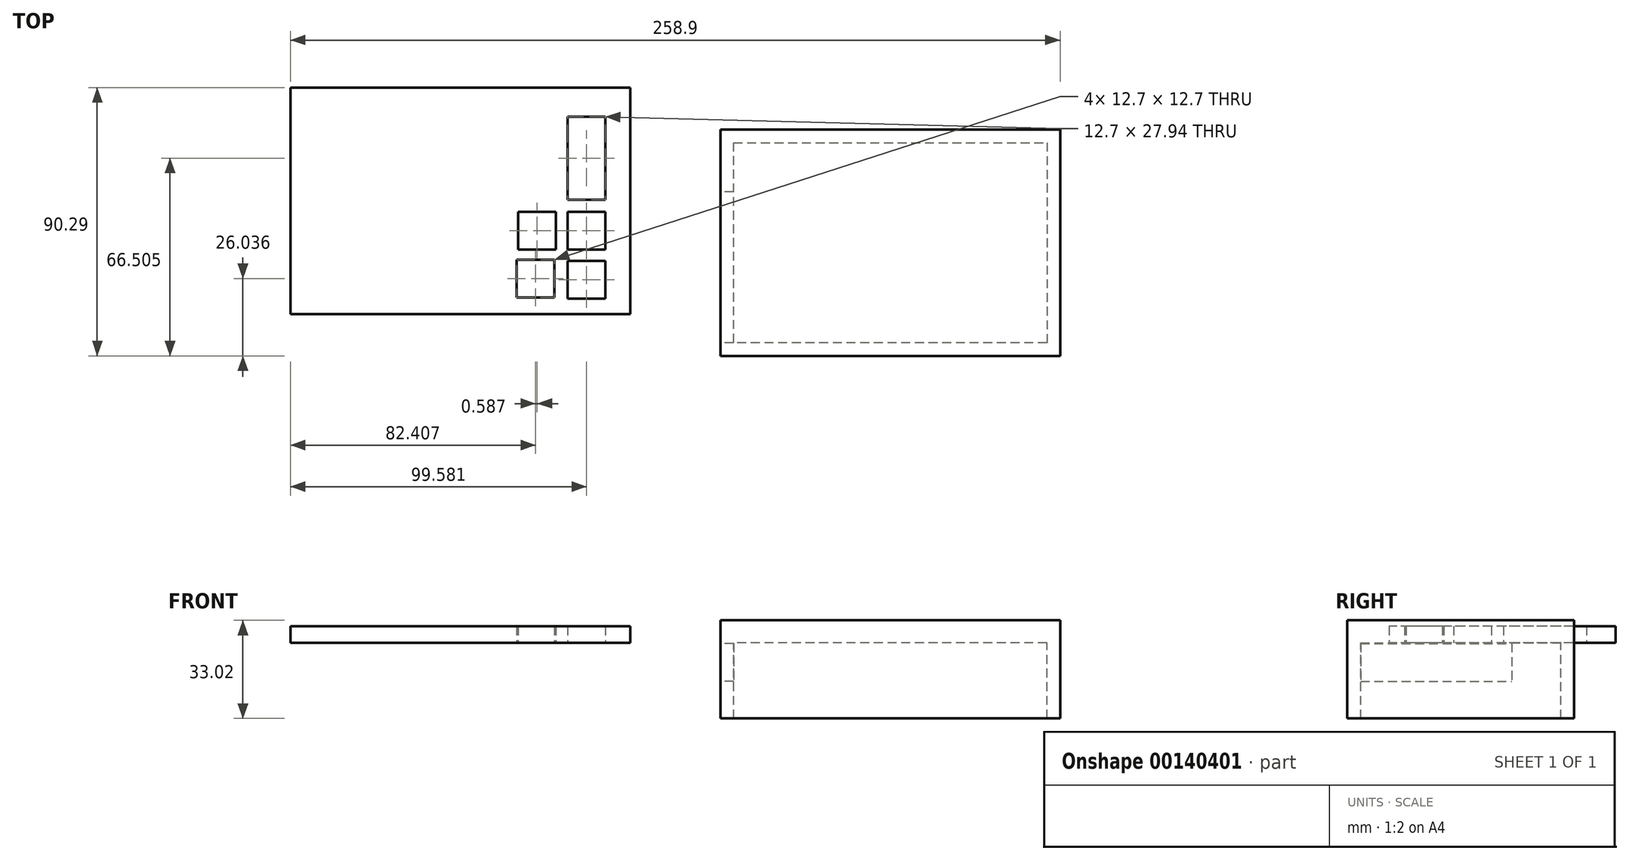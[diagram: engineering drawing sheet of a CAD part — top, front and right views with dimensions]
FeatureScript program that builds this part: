
annotation { "Feature Type Name" : "Feature", "Feature Type Description" : "" }
export const myFeature = defineFeature(function(context is Context, id is Id, definition is map)
    precondition{}
    {
        {
            var Q0;
            Q0=qCreatedBy(makeId("Top.planeOp"),FACE);
            var sketch = newSketch(context, id + "F0", { "sketchPlane" : qUnion([Q0])});
            skLineSegment(sketch, "E0.bottom", {"start": v(-47.68, 26.1) * mm, "end": v(66.62, 26.1) * mm});
            skLineSegment(sketch, "E0.top", {"start": v(-47.68, -50.1) * mm, "end": v(66.62, -50.1) * mm});
            skLineSegment(sketch, "E0.left", {"start": v(-47.68, 26.1) * mm, "end": v(-47.68, -50.1) * mm});
            skLineSegment(sketch, "E0.right", {"start": v(66.62, 26.1) * mm, "end": v(66.62, -50.1) * mm});
            skSolve(sketch);
        }
        {
            var Q0;
            Q0=makeQuery(id+"F0.imprint","IMPRINT",FACE,{"disambiguationData":[TD([[makeQuery(id+"F0.imprint","IMPRINT",EDGE,{"derivedFrom":sQuery(id+"F0.wireOp",EDGE,"E0.bottom")}),-1.0]])]});
            extrude(context, id + "F1", {"entities" : qUnion([Q0]), "depth" : 7.62 * mm});
        }
        {
            var Q0;
            Q0=makeQuery(id+"F1.opExtrude","CAP_FACE",FACE,{"disambiguationData":[OSD([sQuery(id+"F0.wireOp",EDGE,"E0.bottom"),sQuery(id+"F0.wireOp",EDGE,"E0.top"),sQuery(id+"F0.wireOp",EDGE,"E0.left"),sQuery(id+"F0.wireOp",EDGE,"E0.right")])],"isStart":true});
            var sketch = newSketch(context, id + "F2", { "sketchPlane" : qUnion([Q0])});
            skLineSegment(sketch, "E1", {"start": v(-47.68, -26.1) * mm, "end": v(-47.68, -23.57) * mm});
            skLineSegment(sketch, "E2", {"start": v(66.62, -26.1) * mm, "end": v(25.98, -26.1) * mm});
            skLineSegment(sketch, "E3", {"start": v(66.62, 50.1) * mm, "end": v(66.62, 45.65) * mm});
            skLineSegment(sketch, "E4", {"start": v(-47.68, 50.1) * mm, "end": v(-43.23, 50.1) * mm});
            skLineSegment(sketch, "E5", {"start": v(-43.23, 45.65) * mm, "end": v(-43.23, -21.66) * mm});
            skLineSegment(sketch, "E6", {"start": v(-43.23, -21.66) * mm, "end": v(62.18, -21.66) * mm});
            skLineSegment(sketch, "E7", {"start": v(62.18, -21.66) * mm, "end": v(62.18, 45.65) * mm});
            skLineSegment(sketch, "E8", {"start": v(62.18, 45.65) * mm, "end": v(-43.23, 45.65) * mm});
            skSolve(sketch);
        }
        {
            var Q0;
            {var subQ3=sQuery(id+"F2.wireOp",EDGE,"E1");Q0=makeQuery(id+"F2.imprint","IMPRINT",FACE,{"disambiguationData":[TD([[makeQuery(id+"F2.imprint","IMPRINT",EDGE,{"derivedFrom":subQ3}),-1.0]])]});}
            extrude(context, id + "F3", {"entities" : qUnion([Q0]), "operationType" : NewBodyOperationType.ADD, "depth" : 25.4 * mm});
        }
        {
            var Q0;
            {var subQ0=sQuery(id+"F0.wireOp",EDGE,"E0.left");Q0=makeQuery(id+"F3.boolean.opBoolean","MERGE",FACE,{"derivedFrom":[makeQuery(id+"F1.opExtrude","SWEPT_FACE",FACE,{"disambiguationData":[OSD([subQ0])]}),makeQuery(id+"F3.opExtrude","SWEPT_FACE",FACE,{"disambiguationData":[OSD([subQ0,sQuery(id+"F2.wireOp",EDGE,"E1")])]})]});}
            var sketch = newSketch(context, id + "F4", { "sketchPlane" : qUnion([Q0])});
            skLineSegment(sketch, "E9.bottom", {"start": v(45.65, -0.18) * mm, "end": v(-5.15, -0.18) * mm});
            skLineSegment(sketch, "E9.top", {"start": v(45.65, -12.88) * mm, "end": v(-5.15, -12.88) * mm});
            skLineSegment(sketch, "E9.left", {"start": v(45.65, -0.18) * mm, "end": v(45.65, -12.88) * mm});
            skLineSegment(sketch, "E9.right", {"start": v(-5.15, -0.18) * mm, "end": v(-5.15, -12.88) * mm});
            skSolve(sketch);
        }
        {
            var Q0;
            Q0 = qSketchRegion(id + "F4", true);
            extrude(context, id + "F5", {"entities" : qUnion([Q0]), "operationType" : NewBodyOperationType.REMOVE, "oppositeDirection" : true, "depth" : 4.44 * mm});
        }
        {
            var Q0;
            Q0=qCreatedBy(makeId("Top.planeOp"),FACE);
            var sketch = newSketch(context, id + "F6", { "sketchPlane" : qUnion([Q0])});
            skLineSegment(sketch, "E10.bottom", {"start": v(-192.28, 40.2) * mm, "end": v(-77.98, 40.2) * mm});
            skLineSegment(sketch, "E10.top", {"start": v(-192.28, -36) * mm, "end": v(-77.98, -36) * mm});
            skLineSegment(sketch, "E10.left", {"start": v(-192.28, 40.2) * mm, "end": v(-192.28, -36) * mm});
            skLineSegment(sketch, "E10.right", {"start": v(-77.98, 40.2) * mm, "end": v(-77.98, -36) * mm});
            skLineSegment(sketch, "E11.bottom", {"start": v(-99.05, 30.38) * mm, "end": v(-86.35, 30.38) * mm});
            skLineSegment(sketch, "E11.top", {"start": v(-99.05, 2.44) * mm, "end": v(-86.35, 2.44) * mm});
            skLineSegment(sketch, "E11.left", {"start": v(-99.05, 30.38) * mm, "end": v(-99.05, 2.44) * mm});
            skLineSegment(sketch, "E11.right", {"start": v(-86.35, 30.38) * mm, "end": v(-86.35, 2.44) * mm});
            skLineSegment(sketch, "E12.bottom", {"start": v(-86.35, -1.6) * mm, "end": v(-99.05, -1.6) * mm});
            skLineSegment(sketch, "E12.top", {"start": v(-86.35, -14.3) * mm, "end": v(-99.05, -14.3) * mm});
            skLineSegment(sketch, "E12.left", {"start": v(-86.35, -1.6) * mm, "end": v(-86.35, -14.3) * mm});
            skLineSegment(sketch, "E12.right", {"start": v(-99.05, -1.6) * mm, "end": v(-99.05, -14.3) * mm});
            skLineSegment(sketch, "E13", {"start": v(-77.98, -36) * mm, "end": v(-77.98, -30.85) * mm});
            skLineSegment(sketch, "E14", {"start": v(-86.35, -30.85) * mm, "end": v(-99.05, -30.85) * mm});
            skLineSegment(sketch, "E15", {"start": v(-99.05, -30.85) * mm, "end": v(-99.05, -18.15) * mm});
            skLineSegment(sketch, "E16", {"start": v(-99.05, -18.15) * mm, "end": v(-86.35, -18.15) * mm});
            skLineSegment(sketch, "E17", {"start": v(-86.35, -18.15) * mm, "end": v(-86.35, -30.85) * mm});
            skLineSegment(sketch, "E18.bottom", {"start": v(-102.94, -1.6) * mm, "end": v(-115.64, -1.6) * mm});
            skLineSegment(sketch, "E18.top", {"start": v(-102.94, -14.3) * mm, "end": v(-115.64, -14.3) * mm});
            skLineSegment(sketch, "E18.left", {"start": v(-102.94, -1.6) * mm, "end": v(-102.94, -14.3) * mm});
            skLineSegment(sketch, "E18.right", {"start": v(-115.64, -1.6) * mm, "end": v(-115.64, -14.3) * mm});
            skLineSegment(sketch, "E19.bottom", {"start": v(-103.52, -17.7) * mm, "end": v(-116.22, -17.7) * mm});
            skLineSegment(sketch, "E19.top", {"start": v(-103.52, -30.4) * mm, "end": v(-116.22, -30.4) * mm});
            skLineSegment(sketch, "E19.left", {"start": v(-103.52, -17.7) * mm, "end": v(-103.52, -30.4) * mm});
            skLineSegment(sketch, "E19.right", {"start": v(-116.22, -17.7) * mm, "end": v(-116.22, -30.4) * mm});
            skSolve(sketch);
        }
        {
            var Q0;
            Q0 = qSketchRegion(id + "F6", true);
            extrude(context, id + "F7", {"entities" : qUnion([Q0]), "depth" : 5.6 * mm});
        }
    });
